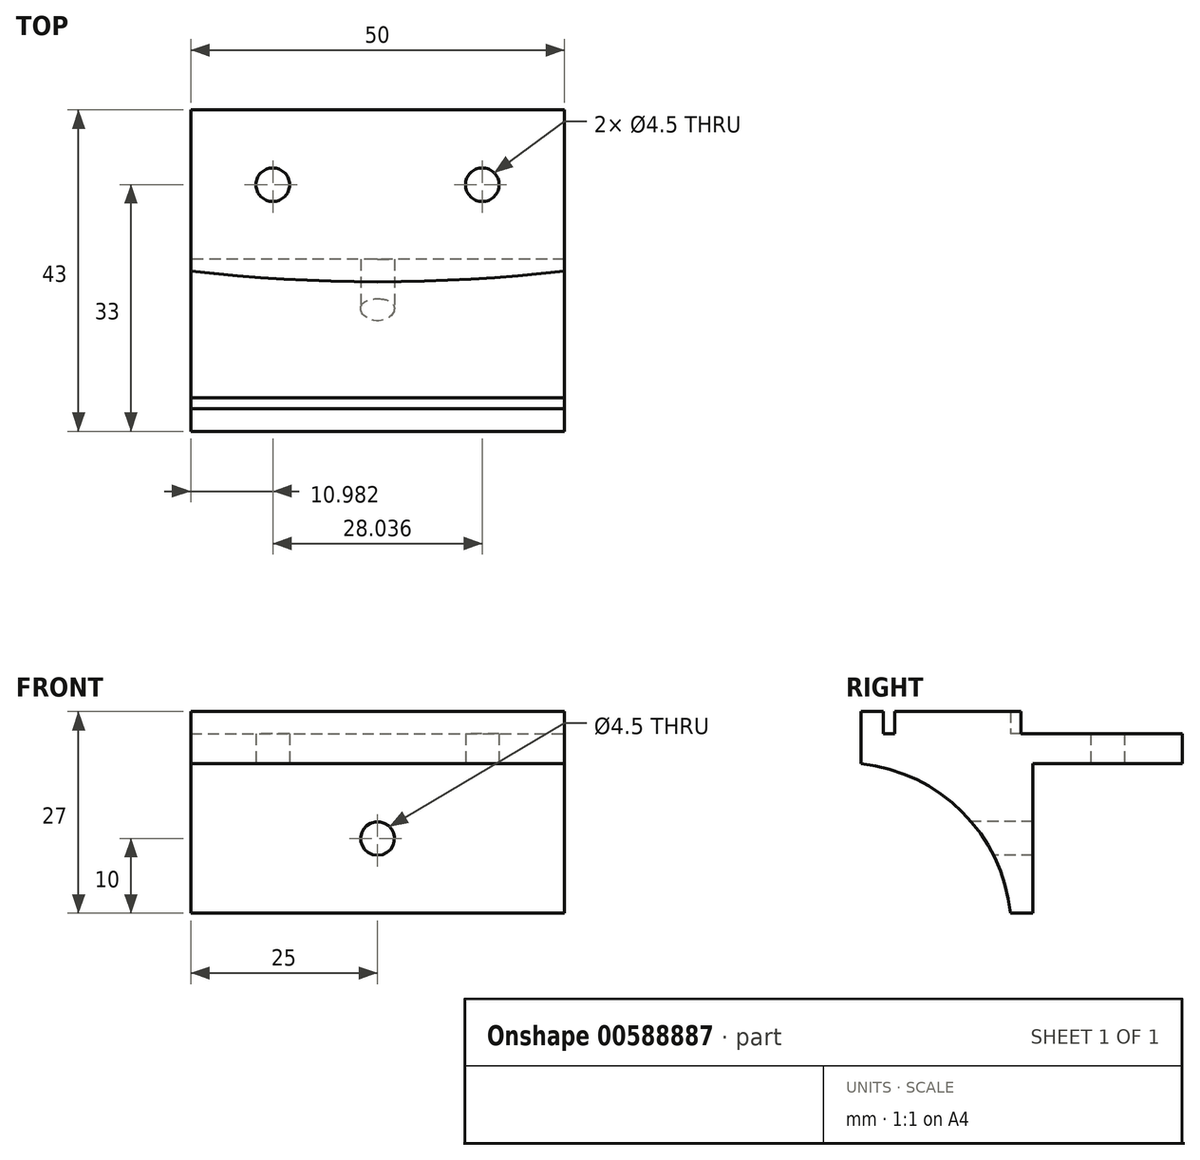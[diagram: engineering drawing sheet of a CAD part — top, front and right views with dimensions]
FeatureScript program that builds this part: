
annotation { "Feature Type Name" : "Feature", "Feature Type Description" : "" }
export const myFeature = defineFeature(function(context is Context, id is Id, definition is map)
    precondition{}
    {
        {
            var Q0;
            Q0=qCreatedBy(makeId("Top.planeOp"),FACE);
            var sketch = newSketch(context, id + "F0", { "sketchPlane" : qUnion([Q0])});
            skArc(sketch, "E0", {"start": v(-25, 21.43) * mm, "mid": v(0, 20) * mm, "end": v(25, 21.43) * mm});
            skPoint(sketch, "E1", {"position": v(0, 20) * mm});
            skLineSegment(sketch, "E2", {"start": v(-25, 21.43) * mm, "end": v(-25, 0) * mm});
            skLineSegment(sketch, "E3", {"start": v(-25, 0) * mm, "end": v(25, 0) * mm});
            skLineSegment(sketch, "E4", {"start": v(25, 0) * mm, "end": v(25, 21.43) * mm});
            skLineSegment(sketch, "E5.bottom", {"start": v(-25, 43) * mm, "end": v(25, 43) * mm});
            skLineSegment(sketch, "E5.left", {"start": v(-25, 43) * mm, "end": v(-25, 0) * mm});
            skLineSegment(sketch, "E5.right", {"start": v(25, 43) * mm, "end": v(25, 0) * mm});
            skCircle(sketch, "E6", {"center": v(-14.02, 33) * mm, "radius": 2.25 * mm});
            skCircle(sketch, "E7.MirrorC", {"center": v(14.02, 33) * mm, "radius": 2.25 * mm});
            skLineSegment(sketch, "E8.bottom", {"start": v(-25, 3) * mm, "end": v(25, 3) * mm});
            skLineSegment(sketch, "E8.top", {"start": v(-25, 4.5) * mm, "end": v(25, 4.5) * mm});
            skLineSegment(sketch, "E8.left", {"start": v(-25, 3) * mm, "end": v(-25, 4.5) * mm});
            skLineSegment(sketch, "E8.right", {"start": v(25, 3) * mm, "end": v(25, 4.5) * mm});
            skSolve(sketch);
        }
        {
            var Q0;
            Q0 = qSketchRegion(id + "F0", true);
            extrude(context, id + "F1", {"entities" : qUnion([Q0]), "depth" : 4 * mm, "offsetDistance" : 25 * mm});
        }
        {
            var Q0;
            {var subQ0=sQuery(id+"F0.wireOp",EDGE,"E0");Q0=makeQuery(id+"F0.imprint","IMPRINT",FACE,{"disambiguationData":[TD([[makeQuery(id+"F0.imprint","IMPRINT",EDGE,{"derivedFrom":subQ0}),-1.0]])]});}
            var Q1;
            {var subQ0=sQuery(id+"F0.wireOp",EDGE,"E3");Q1=makeQuery(id+"F0.imprint","IMPRINT",FACE,{"disambiguationData":[TD([[makeQuery(id+"F0.imprint","IMPRINT",EDGE,{"derivedFrom":subQ0}),1.0]])]});}
            extrude(context, id + "F2", {"entities" : qUnion([Q0, Q1]), "operationType" : NewBodyOperationType.ADD, "depth" : 7 * mm, "offsetDistance" : 25 * mm});
        }
        {
            var Q0;
            Q0=qCreatedBy(makeId("Right.planeOp"),FACE);
            var sketch = newSketch(context, id + "F3", { "sketchPlane" : qUnion([Q0])});
            skPoint(sketch, "E9.0", {"position": v(0, 0) * mm});
            skPoint(sketch, "E10.0", {"position": v(3, 0) * mm});
            skPoint(sketch, "E11.0", {"position": v(4.5, 0) * mm});
            skPoint(sketch, "E12.0", {"position": v(43, 0) * mm});
            skPoint(sketch, "E13.0", {"position": v(21.43, 0) * mm});
            skPoint(sketch, "E14.0", {"position": v(4.5, 7) * mm});
            skPoint(sketch, "E15.0", {"position": v(3, 7) * mm});
            skPoint(sketch, "E16.0", {"position": v(3, 4) * mm});
            skPoint(sketch, "E17.0", {"position": v(4.5, 4) * mm});
            skPoint(sketch, "E18.0", {"position": v(0, 7) * mm});
            skPoint(sketch, "E19.0", {"position": v(21.43, 7) * mm});
            skPoint(sketch, "E20.0", {"position": v(21.43, 4) * mm});
            skPoint(sketch, "E21.0", {"position": v(43, 4) * mm});
            skLineSegment(sketch, "E22", {"start": v(0, 7) * mm, "end": v(3, 7) * mm});
            skLineSegment(sketch, "E23", {"start": v(3, 4) * mm, "end": v(3, 7) * mm});
            skLineSegment(sketch, "E24", {"start": v(3, 4) * mm, "end": v(4.5, 4) * mm});
            skLineSegment(sketch, "E25", {"start": v(4.5, 7) * mm, "end": v(21.43, 7) * mm});
            skLineSegment(sketch, "E26", {"start": v(21.43, 4) * mm, "end": v(43, 4) * mm});
            skLineSegment(sketch, "E27", {"start": v(43, 0) * mm, "end": v(43, 4) * mm});
            skLineSegment(sketch, "E28", {"start": v(43, 0) * mm, "end": v(0, 0) * mm});
            skLineSegment(sketch, "E29", {"start": v(0, 0) * mm, "end": v(0, 7) * mm});
            skLineSegment(sketch, "E30", {"start": v(4.5, 7) * mm, "end": v(4.5, 4) * mm});
            skLineSegment(sketch, "E31", {"start": v(21.43, 7) * mm, "end": v(21.43, 4) * mm});
            skPoint(sketch, "E32", {"position": v(23, 0) * mm});
            skLineSegment(sketch, "E33", {"start": v(23, 0) * mm, "end": v(23, -20) * mm});
            skLineSegment(sketch, "E34", {"start": v(23, -20) * mm, "end": v(20, -20) * mm});
            skArc(sketch, "E35", {"start": v(20, -20) * mm, "mid": v(13.56, -6.44) * mm, "end": v(0, 0) * mm});
            skSolve(sketch);
        }
        {
            var Q0;
            {var subQ2=sQuery(id+"F3.wireOp",EDGE,"E33");Q0=makeQuery(id+"F3.imprint","IMPRINT",FACE,{"disambiguationData":[TD([[makeQuery(id+"F3.imprint","IMPRINT",EDGE,{"derivedFrom":subQ2}),-1.0]])]});}
            var Q1;
            {var subQ0=sQuery(id+"F0.wireOp",EDGE,"E5.right");var subQ1=sQuery(id+"F0.wireOp",EDGE,"E8.right");Q1=makeQuery(id+"F2.boolean.opBoolean","MERGE",FACE,{"derivedFrom":[makeQuery(id+"F1.opExtrude","SWEPT_FACE",FACE,{"disambiguationData":[OSD([subQ0,subQ1])]}),makeQuery(id+"F2.opExtrude","SWEPT_FACE",FACE,{"disambiguationData":[OSD([subQ0]),TDD([makeQuery(id+"F0.imprint","IMPRINT",EDGE,{"disambiguationData":[TD([[makeQuery(id+"F0.imprint","INTERSECT",VERTEX,{"derivedFrom":[sQuery(id+"F0.wireOp",EDGE,"E0"),subQ0]}),-1.0]])],"derivedFrom":subQ0})])]}),makeQuery(id+"F2.opExtrude","SWEPT_FACE",FACE,{"disambiguationData":[OSD([subQ0]),TDD([makeQuery(id+"F0.imprint","IMPRINT",EDGE,{"disambiguationData":[TD([[makeQuery(id+"F0.imprint","INTERSECT",VERTEX,{"derivedFrom":[sQuery(id+"F0.wireOp",EDGE,"E3"),subQ0]}),1.0]])],"derivedFrom":subQ0})])]})]});}
            var Q2;
            {var subQ0=sQuery(id+"F0.wireOp",EDGE,"E5.left");var subQ1=sQuery(id+"F0.wireOp",EDGE,"E8.left");Q2=makeQuery(id+"F2.boolean.opBoolean","MERGE",FACE,{"derivedFrom":[makeQuery(id+"F1.opExtrude","SWEPT_FACE",FACE,{"disambiguationData":[OSD([subQ0,subQ1])]}),makeQuery(id+"F2.opExtrude","SWEPT_FACE",FACE,{"disambiguationData":[OSD([subQ0]),TDD([makeQuery(id+"F0.imprint","IMPRINT",EDGE,{"disambiguationData":[TD([[makeQuery(id+"F0.imprint","INTERSECT",VERTEX,{"derivedFrom":[sQuery(id+"F0.wireOp",EDGE,"E0"),subQ0]}),-1.0]])],"derivedFrom":subQ0})])]}),makeQuery(id+"F2.opExtrude","SWEPT_FACE",FACE,{"disambiguationData":[OSD([subQ0]),TDD([makeQuery(id+"F0.imprint","IMPRINT",EDGE,{"disambiguationData":[TD([[makeQuery(id+"F0.imprint","INTERSECT",VERTEX,{"derivedFrom":[sQuery(id+"F0.wireOp",EDGE,"E3"),subQ0]}),1.0]])],"derivedFrom":subQ0})])]})]});}
            extrude(context, id + "F4", {"entities" : qUnion([Q0]), "operationType" : NewBodyOperationType.ADD, "endBound" : BoundingType.UP_TO_SURFACE, "depth" : 25 * mm, "endBoundEntityFace" : qUnion([Q1]), "offsetDistance" : 25 * mm, "hasSecondDirection" : true, "secondDirectionBound" : SecondDirectionBoundingType.UP_TO_SURFACE, "secondDirectionOppositeDirection" : true, "secondDirectionDepth" : 25 * mm, "secondDirectionBoundEntityFace" : qUnion([Q2])});
        }
        {
            var Q0;
            Q0=qCreatedBy(makeId("Right.planeOp"),FACE);
            var sketch = newSketch(context, id + "F5", { "sketchPlane" : qUnion([Q0])});
            skLineSegment(sketch, "E36.bottom", {"start": v(-3.62, 10) * mm, "end": v(33.88, 10) * mm});
            skLineSegment(sketch, "E36.top", {"start": v(-3.62, -22.06) * mm, "end": v(33.88, -22.06) * mm});
            skLineSegment(sketch, "E36.left", {"start": v(-3.62, 10) * mm, "end": v(-3.62, -22.06) * mm});
            skLineSegment(sketch, "E36.right", {"start": v(33.88, 10) * mm, "end": v(33.88, -22.06) * mm});
            skSolve(sketch);
        }
        {
            var Q0;
            Q0=qCreatedBy(makeId("Front.planeOp"),FACE);
            var sketch = newSketch(context, id + "F6", { "sketchPlane" : qUnion([Q0])});
            skPoint(sketch, "E37.0", {"position": v(-25, 7) * mm});
            skPoint(sketch, "E38.0", {"position": v(25, 7) * mm});
            skPoint(sketch, "E39.0", {"position": v(25, -20) * mm});
            skPoint(sketch, "E40.0", {"position": v(-25, -20) * mm});
            skLineSegment(sketch, "E41", {"start": v(-25, 7) * mm, "end": v(-25, -20) * mm});
            skLineSegment(sketch, "E42", {"start": v(25, -20) * mm, "end": v(25, 7) * mm});
            skCircle(sketch, "E43", {"center": v(0, -10) * mm, "radius": 2.25 * mm});
            skCircle(sketch, "E44", {"center": v(0, -10) * mm, "radius": 3.75 * mm});
            skSolve(sketch);
        }
        {
            var Q0;
            Q0=makeQuery(id+"F6.imprint","IMPRINT",FACE,{"disambiguationData":[TD([[makeQuery(id+"F6.imprint","IMPRINT",EDGE,{"derivedFrom":sQuery(id+"F6.wireOp",EDGE,"E43")}),1.0]])]});
            var Q1;
            Q1=sQuery(id+"F6.wireOp",EDGE,"E44");
            var Q2;
            Q2=makeQuery(id+"F4.opExtrude","SWEPT_FACE",FACE,{"disambiguationData":[OSD([sQuery(id+"F3.wireOp",EDGE,"E33")])]});
            extrude(context, id + "F7", {"entities" : qUnion([Q0]), "operationType" : NewBodyOperationType.REMOVE, "surfaceEntities" : qUnion([Q1]), "endBound" : BoundingType.UP_TO_SURFACE, "oppositeDirection" : true, "depth" : 25 * mm, "endBoundEntityFace" : qUnion([Q2]), "offsetDistance" : 25 * mm});
        }
        {
            var Q0;
            Q0=makeQuery(id+"F6.imprint","IMPRINT",FACE,{"disambiguationData":[TD([[makeQuery(id+"F6.imprint","IMPRINT",EDGE,{"derivedFrom":sQuery(id+"F6.wireOp",EDGE,"E43")}),-1.0]])]});
            extrude(context, id + "F8", {"entities" : qUnion([Q0]), "operationType" : NewBodyOperationType.REMOVE, "oppositeDirection" : true, "depth" : 10 * mm, "offsetDistance" : 25 * mm});
        }
    });
